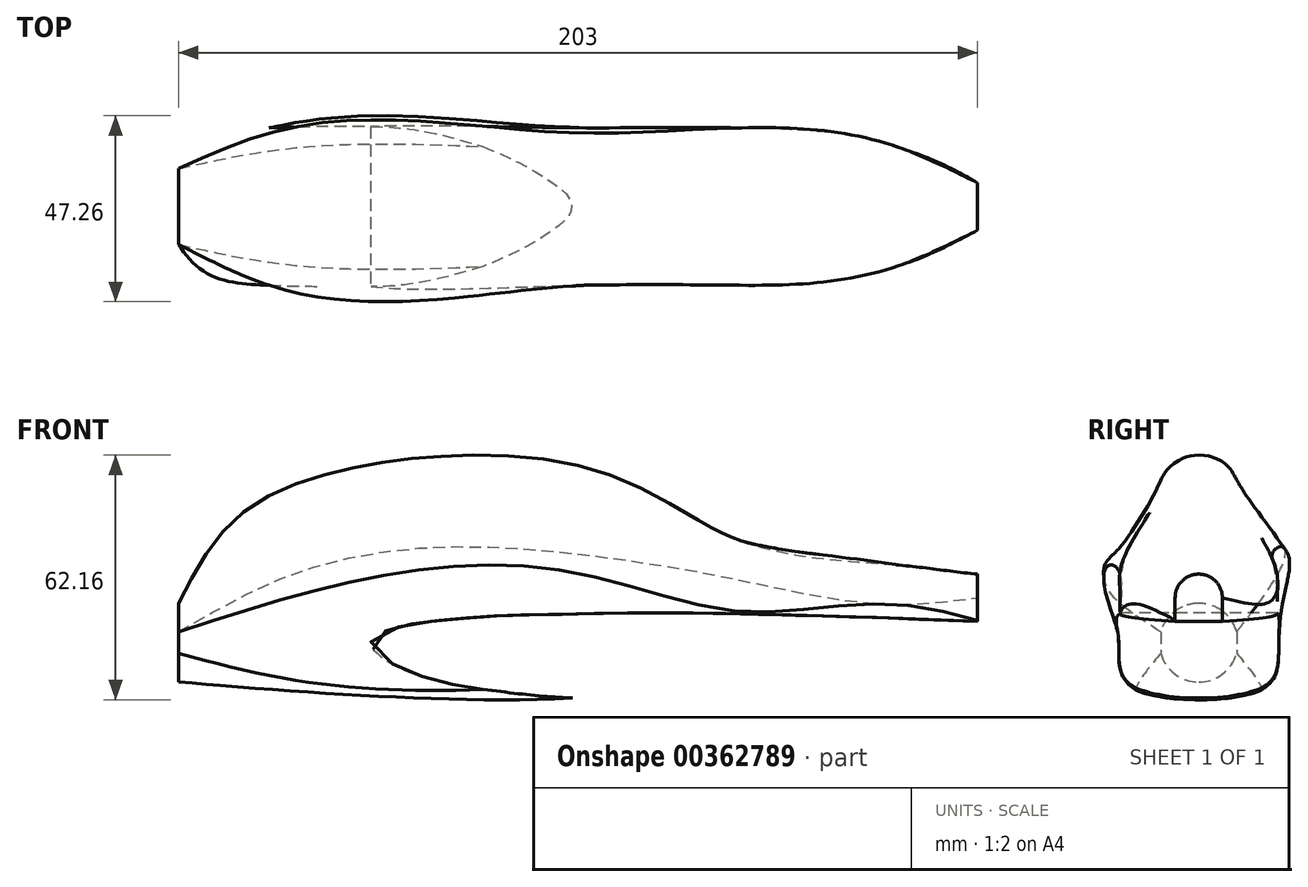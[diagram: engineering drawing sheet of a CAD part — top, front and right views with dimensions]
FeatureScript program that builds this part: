
annotation { "Feature Type Name" : "Feature", "Feature Type Description" : "" }
export const myFeature = defineFeature(function(context is Context, id is Id, definition is map)
    precondition{}
    {
        {
            var Q0;
            Q0=qCreatedBy(makeId("Front.planeOp"),FACE);
            var sketch = newSketch(context, id + "F0", { "sketchPlane" : qUnion([Q0])});
            skLineSegment(sketch, "E0", {"start": v(0, 0) * mm, "end": v(80, 0) * mm});
            skLineSegment(sketch, "E1", {"start": v(80, 0) * mm, "end": v(120, 0) * mm});
            skLineSegment(sketch, "E2", {"start": v(120, 0) * mm, "end": v(160, 0) * mm});
            skLineSegment(sketch, "E3", {"start": v(0, 0) * mm, "end": v(-23, 0) * mm});
            skFitSpline(sketch, "E4.MirrorC", {"points": [v(25.84, 0.14) * mm, v(26.2, -1.34) * mm, v(27.08, -2.35) * mm, v(28.33, -3.55) * mm, v(30.08, -4.7) * mm, v(32.8, -6.23) * mm, v(35.46, -7.4) * mm, v(38.11, -8.38) * mm, v(44.79, -10.16) * mm, v(48.42, -10.93) * mm, v(53, -11.66) * mm, v(60.13, -12.6) * mm, v(65.7, -13.23) * mm, v(74.41, -13.95) * mm, v(88.1, -14.27) * mm, v(105.53, -14.11) * mm, v(121.93, -13.31) * mm, v(140.09, -12.11) * mm, v(156.97, -10.83) * mm, v(169.9, -9.7) * mm, v(184.03, -8.35) * mm, v(203.13, -6.33) * mm, v(218.47, -4.65) * mm, v(234.68, -3.1) * mm, v(252.9, -1.42) * mm, v(264.8, -0.42) * mm, v(275.84, 0.12) * mm, v(266.91, 0.53) * mm, v(261.43, 0.73) * mm, v(246.9, 1.7) * mm, v(235.2, 2.49) * mm, v(226.11, 3) * mm, v(209.6, 3.97) * mm, v(191.03, 4.88) * mm, v(170.07, 5.75) * mm, v(159.92, 6.16) * mm, v(136, 6.9) * mm, v(118.1, 7.34) * mm, v(93.27, 7.6) * mm, v(84.17, 7.42) * mm, v(60.8, 6.9) * mm, v(51, 6.34) * mm, v(44.7, 5.78) * mm, v(38.68, 5.1) * mm, v(33.53, 4.18) * mm, v(29.5, 2.94) * mm, v(27.61, 2.16) * mm, v(26.44, 1.4) * mm, v(25.84, 0.14) * mm]});
            skLineSegment(sketch, "E5", {"start": v(160, 0) * mm, "end": v(180, 0) * mm});
            skSolve(sketch);
        }
        {
            var Q0;
            Q0=sQuery(id+"F0.wireOp",EDGE,"E0");
            var Q1;
            Q1=sQuery(id+"F0.wireOp",VERTEX,"E1.start");
            cPlane(context, id + "F1", {"entities" : qUnion([Q0, Q1]), "cplaneType" : CPlaneType.LINE_POINT, "offset" : 25 * mm, "width" : 150 * mm, "height" : 150 * mm});
        }
        {
            var Q0;
            Q0=sQuery(id+"F0.wireOp",EDGE,"E1");
            var Q1;
            Q1=sQuery(id+"F0.wireOp",VERTEX,"E2.start");
            cPlane(context, id + "F2", {"entities" : qUnion([Q0, Q1]), "cplaneType" : CPlaneType.LINE_POINT, "offset" : 25 * mm, "width" : 150 * mm, "height" : 150 * mm});
        }
        {
            var Q0;
            Q0=sQuery(id+"F0.wireOp",EDGE,"E2");
            var Q1;
            Q1=sQuery(id+"F0.wireOp",VERTEX,"E2.end");
            cPlane(context, id + "F3", {"entities" : qUnion([Q0, Q1]), "cplaneType" : CPlaneType.LINE_POINT, "offset" : 25 * mm, "width" : 150 * mm, "height" : 150 * mm});
        }
        {
            var Q0;
            Q0=sQuery(id+"F0.wireOp",EDGE,"E3");
            var Q1;
            Q1=sQuery(id+"F0.wireOp",VERTEX,"E3.end");
            cPlane(context, id + "F4", {"entities" : qUnion([Q0, Q1]), "cplaneType" : CPlaneType.LINE_POINT, "offset" : 25 * mm, "width" : 150 * mm, "height" : 150 * mm});
        }
        {
            var Q0;
            Q0=qCreatedBy(id+"F4.planeOp",FACE);
            var sketch = newSketch(context, id + "F5", { "sketchPlane" : qUnion([Q0])});
            skArc(sketch, "E6", {"start": v(0, 10) * mm, "mid": v(-6.04, 7.97) * mm, "end": v(-9.63, 2.7) * mm});
            skArc(sketch, "E7", {"start": v(0, -10) * mm, "mid": v(-6.04, -7.97) * mm, "end": v(-9.63, -2.7) * mm});
            skLineSegment(sketch, "E8", {"start": v(-9.63, 2.7) * mm, "end": v(-9.63, -2.7) * mm});
            skPoint(sketch, "E9", {"position": v(-9.63, 0) * mm});
            skPoint(sketch, "E9.positionSnap0", {"position": v(-9.63, 0) * mm});
            skArc(sketch, "E10.MirrorCS", {"start": v(0, -10) * mm, "mid": v(6.04, -7.97) * mm, "end": v(9.63, -2.7) * mm});
            skLineSegment(sketch, "E11.MirrorCS", {"start": v(9.63, 2.7) * mm, "end": v(9.63, -2.7) * mm});
            skArc(sketch, "E12.MirrorCS", {"start": v(0, 10) * mm, "mid": v(6.04, 7.97) * mm, "end": v(9.63, 2.7) * mm});
            skSolve(sketch);
        }
        {
            var Q0;
            Q0=qCreatedBy(makeId("Right.planeOp"),FACE);
            var sketch = newSketch(context, id + "F6", { "sketchPlane" : qUnion([Q0])});
            skArc(sketch, "E13", {"start": v(20, 10) * mm, "mid": v(19.66, 12.59) * mm, "end": v(18.66, 15) * mm});
            skArc(sketch, "E14", {"start": v(8.66, 32.32) * mm, "mid": v(5, 35.98) * mm, "end": v(0, 37.32) * mm});
            skLineSegment(sketch, "E15", {"start": v(18.66, 15) * mm, "end": v(8.66, 32.32) * mm});
            skLineSegment(sketch, "E16", {"start": v(20, 0) * mm, "end": v(20, 10) * mm});
            skEllipticalArc(sketch, "E17", {});
            skPoint(sketch, "E18", {"position": v(0, 37.32) * mm});
            skPoint(sketch, "E19.end.orphan", {"position": v(-20, 0) * mm});
            skPoint(sketch, "E20.center.orphan", {"position": v(-10, 10) * mm});
            skEllipticalArc(sketch, "E21.MirrorCS", {});
            skLineSegment(sketch, "E22.MirrorCS", {"start": v(-20, 0) * mm, "end": v(-20, 10) * mm});
            skArc(sketch, "E23.MirrorCS", {"start": v(-20, 10) * mm, "mid": v(-19.66, 12.59) * mm, "end": v(-18.66, 15) * mm});
            skLineSegment(sketch, "E24.MirrorCS", {"start": v(-18.66, 15) * mm, "end": v(-8.66, 32.32) * mm});
            skArc(sketch, "E25.MirrorCS", {"start": v(-8.66, 32.32) * mm, "mid": v(-5, 35.98) * mm, "end": v(0, 37.32) * mm});
            const initialGuessF6  = {"E17": [0, 0, -1, 0, 0.02, 0.011848411419733682, 1.5707963267948966, 3.141592653589793], "E21.MirrorCS": [0, 0, 1, 0, 0.02, 0.011848411419733682, 3.141592653589793, 4.71238898038469]};
            skSetInitialGuess(sketch, initialGuessF6);
            skSolve(sketch);
        }
        {
            var Q0;
            Q0=qCreatedBy(id+"F1.planeOp",FACE);
            var sketch = newSketch(context, id + "F7", { "sketchPlane" : qUnion([Q0])});
            skArc(sketch, "E26", {"start": v(20, 17.34) * mm, "mid": v(19.66, 19.93) * mm, "end": v(18.66, 22.34) * mm});
            skArc(sketch, "E27", {"start": v(8.66, 39.66) * mm, "mid": v(5, 43.32) * mm, "end": v(0, 44.66) * mm});
            skLineSegment(sketch, "E28", {"start": v(18.66, 22.34) * mm, "end": v(8.66, 39.66) * mm});
            skLineSegment(sketch, "E29", {"start": v(20, 0) * mm, "end": v(20, 17.34) * mm});
            skPoint(sketch, "E30", {"position": v(0, 0) * mm});
            skPoint(sketch, "E31", {"position": v(0, 7.34) * mm});
            skEllipticalArc(sketch, "E32", {});
            skPoint(sketch, "E33", {"position": v(0, 44.66) * mm});
            skPoint(sketch, "E34.end.orphan", {"position": v(-20, 0) * mm});
            skEllipticalArc(sketch, "E35.MirrorCS", {});
            skLineSegment(sketch, "E36.MirrorCS", {"start": v(-20, 0) * mm, "end": v(-20, 17.34) * mm});
            skArc(sketch, "E37.MirrorCS", {"start": v(-20, 17.34) * mm, "mid": v(-19.66, 19.93) * mm, "end": v(-18.66, 22.34) * mm});
            skLineSegment(sketch, "E38.MirrorCS", {"start": v(-18.66, 22.34) * mm, "end": v(-8.66, 39.66) * mm});
            skArc(sketch, "E39.MirrorCS", {"start": v(-8.66, 39.66) * mm, "mid": v(-5, 43.32) * mm, "end": v(0, 44.66) * mm});
            const initialGuessF7  = {"E32": [0, 0, 1, 0, 0.02, 0.013871131549420329, 4.71238898038469, 0], "E35.MirrorCS": [0, 0, -1, 0, 0.02, 0.013871131549420329, 0, 1.5707963267948966]};
            skSetInitialGuess(sketch, initialGuessF7);
            skSolve(sketch);
        }
        {
            var Q0;
            Q0=qCreatedBy(id+"F2.planeOp",FACE);
            var sketch = newSketch(context, id + "F8", { "sketchPlane" : qUnion([Q0])});
            skLineSegment(sketch, "E40", {"start": v(0, 25.82) * mm, "end": v(10, 25.82) * mm});
            skLineSegment(sketch, "E41", {"start": v(20, 15.82) * mm, "end": v(20, 0) * mm});
            skPoint(sketch, "E42", {"position": v(0, 0) * mm});
            skArc(sketch, "E43", {"start": v(20, 15.82) * mm, "mid": v(17.07, 22.89) * mm, "end": v(10, 25.82) * mm});
            skPoint(sketch, "E44.orphan", {"position": v(20, 25.82) * mm});
            skPoint(sketch, "E45.orphan", {"position": v(-20, 25.82) * mm});
            skPoint(sketch, "E46.start.orphan", {"position": v(-20, 0) * mm});
            skPoint(sketch, "E47.orphan", {"position": v(-10, 25.82) * mm});
            skEllipticalArc(sketch, "E48", {});
            skEllipticalArc(sketch, "E49.MirrorCS", {});
            skLineSegment(sketch, "E50.MirrorCS", {"start": v(-20, 15.82) * mm, "end": v(-20, 0) * mm});
            skArc(sketch, "E51.MirrorCS", {"start": v(-20, 15.82) * mm, "mid": v(-17.07, 22.89) * mm, "end": v(-10, 25.82) * mm});
            skLineSegment(sketch, "E52.MirrorCS", {"start": v(0, 25.82) * mm, "end": v(-10, 25.82) * mm});
            const initialGuessF8  = {"E48": [0, 0, 1, 0, 0.02, 0.007889031401392533, 4.71238898038469, 0], "E49.MirrorCS": [0, 0, -1, 0, 0.02, 0.007889031401392533, 0, 1.5707963267948966]};
            skSetInitialGuess(sketch, initialGuessF8);
            skSolve(sketch);
        }
        {
            var Q0;
            Q0=qCreatedBy(id+"F3.planeOp",FACE);
            var sketch = newSketch(context, id + "F9", { "sketchPlane" : qUnion([Q0])});
            skLineSegment(sketch, "E53", {"start": v(0, 19.7) * mm, "end": v(5, 19.7) * mm});
            skLineSegment(sketch, "E54", {"start": v(15, 9.7) * mm, "end": v(15, 0) * mm});
            skPoint(sketch, "E55", {"position": v(0, 0) * mm});
            skArc(sketch, "E56", {"start": v(15, 9.7) * mm, "mid": v(12.07, 16.76) * mm, "end": v(5, 19.7) * mm});
            skPoint(sketch, "E57.start.orphan", {"position": v(-15, 0) * mm});
            skPoint(sketch, "E58.orphan", {"position": v(-5, 19.7) * mm});
            skEllipticalArc(sketch, "E59", {});
            skEllipticalArc(sketch, "E60.MirrorCS", {});
            skLineSegment(sketch, "E61.MirrorCS", {"start": v(-15, 9.7) * mm, "end": v(-15, 0) * mm});
            skArc(sketch, "E62.MirrorCS", {"start": v(-15, 9.7) * mm, "mid": v(-12.07, 16.76) * mm, "end": v(-5, 19.7) * mm});
            skLineSegment(sketch, "E63.MirrorCS", {"start": v(0, 19.7) * mm, "end": v(-5, 19.7) * mm});
            const initialGuessF9  = {"E59": [0, 0, 1, 0, 0.015, 0.0073381839387434, 4.71238898038469, 0], "E60.MirrorCS": [0, 0, -1, 0, 0.015, 0.0073381839387434, 0, 1.5707963267948966]};
            skSetInitialGuess(sketch, initialGuessF9);
            skSolve(sketch);
        }
        {
            var Q0;
            Q0=sQuery(id+"F0.wireOp",EDGE,"E5");
            var Q1;
            Q1=sQuery(id+"F0.wireOp",VERTEX,"E5.end");
            cPlane(context, id + "F10", {"entities" : qUnion([Q0, Q1]), "cplaneType" : CPlaneType.LINE_POINT, "offset" : 25 * mm, "width" : 150 * mm, "height" : 150 * mm});
        }
        {
            var Q0;
            Q0=qCreatedBy(id+"F10.planeOp",FACE);
            var sketch = newSketch(context, id + "F11", { "sketchPlane" : qUnion([Q0])});
            skArc(sketch, "E64", {"start": v(6, 11.41) * mm, "mid": v(4.24, 15.65) * mm, "end": v(0, 17.41) * mm});
            skLineSegment(sketch, "E65", {"start": v(6, 0) * mm, "end": v(6, 11.41) * mm});
            skArc(sketch, "E66", {"start": v(0, -6) * mm, "mid": v(4.24, -4.24) * mm, "end": v(6, 0) * mm});
            skArc(sketch, "E67.MirrorCS", {"start": v(0, -6) * mm, "mid": v(-4.24, -4.24) * mm, "end": v(-6, 0) * mm});
            skLineSegment(sketch, "E68.MirrorCS", {"start": v(-6, 0) * mm, "end": v(-6, 11.41) * mm});
            skArc(sketch, "E69.MirrorCS", {"start": v(-6, 11.41) * mm, "mid": v(-4.24, 15.65) * mm, "end": v(0, 17.41) * mm});
            skSolve(sketch);
        }
        {
            var Q0;
            Q0=qCreatedBy(makeId("Top.planeOp"),FACE);
            var sketch = newSketch(context, id + "F12", { "sketchPlane" : qUnion([Q0])});
            skFitSpline(sketch, "E70", {"points": [v(-23, 9.63) * mm, v(0, 20) * mm, v(80, 20) * mm, v(120, 20) * mm, v(160, 15) * mm, v(180, 6) * mm], "startDerivative": vector(109.79, 168.65) * mm, "endDerivative": vector(136.65, -101.2) * mm});
            skFitSpline(sketch, "E71.MirrorCS", {"points": [v(-23, -9.63) * mm, v(0, -20) * mm, v(80, -20) * mm, v(120, -20) * mm, v(160, -15) * mm, v(180, -6) * mm], "startDerivative": vector(109.79, -168.65) * mm, "endDerivative": vector(136.65, 101.2) * mm});
            skSolve(sketch);
        }
        {
            var Q0;
            Q0=qCreatedBy(makeId("Front.planeOp"),FACE);
            var sketch = newSketch(context, id + "F13", { "sketchPlane" : qUnion([Q0])});
            skFitSpline(sketch, "E72", {"points": [v(-23, -10) * mm, v(0, -11.85) * mm, v(80, -13.87) * mm, v(120, -7.89) * mm, v(160, -7.34) * mm, v(180, -6) * mm], "startDerivative": vector(131.62, -10.02) * mm, "endDerivative": vector(123.76, 18.36) * mm});
            skFitSpline(sketch, "E73", {"points": [v(-23, 10) * mm, v(0, 37.32) * mm, v(80, 44.66) * mm, v(120, 25.82) * mm, v(160, 19.7) * mm, v(180, 17.41) * mm], "startDerivative": vector(93.32, 179.4) * mm, "endDerivative": vector(141.15, -12.46) * mm});
            skSolve(sketch);
        }
        {
            var Q0;
            Q0=makeQuery(id+"F5.imprint","IMPRINT",FACE,{"disambiguationData":[TD([[makeQuery(id+"F5.imprint","IMPRINT",EDGE,{"derivedFrom":sQuery(id+"F5.wireOp",EDGE,"E6")}),1.0]])]});
            var Q1;
            Q1=makeQuery(id+"F6.imprint","IMPRINT",FACE,{"disambiguationData":[TD([[makeQuery(id+"F6.imprint","IMPRINT",EDGE,{"derivedFrom":sQuery(id+"F6.wireOp",EDGE,"E13")}),1.0]])]});
            var Q2;
            Q2=makeQuery(id+"F7.imprint","IMPRINT",FACE,{"disambiguationData":[TD([[makeQuery(id+"F7.imprint","IMPRINT",EDGE,{"derivedFrom":sQuery(id+"F7.wireOp",EDGE,"E26")}),1.0]])]});
            var Q3;
            Q3=makeQuery(id+"F8.imprint","IMPRINT",FACE,{"disambiguationData":[TD([[makeQuery(id+"F8.imprint","IMPRINT",EDGE,{"derivedFrom":sQuery(id+"F8.wireOp",EDGE,"E40")}),-1.0]])]});
            var Q4;
            Q4=makeQuery(id+"F9.imprint","IMPRINT",FACE,{"disambiguationData":[TD([[makeQuery(id+"F9.imprint","IMPRINT",EDGE,{"derivedFrom":sQuery(id+"F9.wireOp",EDGE,"E53")}),-1.0]])]});
            var Q5;
            Q5=makeQuery(id+"F11.imprint","IMPRINT",FACE,{"disambiguationData":[TD([[makeQuery(id+"F11.imprint","IMPRINT",EDGE,{"derivedFrom":sQuery(id+"F11.wireOp",EDGE,"E64")}),1.0]])]});
            var Q6;
            Q6=sQuery(id+"F12.wireOp",EDGE,"E71.MirrorCS");
            var Q7;
            Q7=sQuery(id+"F12.wireOp",EDGE,"E70");
            var Q8;
            Q8=sQuery(id+"F13.wireOp",EDGE,"E72");
            var Q9;
            Q9=sQuery(id+"F13.wireOp",EDGE,"E73");
            loft(context, id + "F14", {"addGuides" : true, "sheetProfilesArray" : [{ "sheetProfileEntities" : qUnion([Q0]) }, { "sheetProfileEntities" : qUnion([Q1]) }, { "sheetProfileEntities" : qUnion([Q2]) }, { "sheetProfileEntities" : qUnion([Q3]) }, { "sheetProfileEntities" : qUnion([Q4]) }, { "sheetProfileEntities" : qUnion([Q5]) }], "guidesArray" : [{ "guideEntities" : qUnion([Q6]), "guideDerivativeType" : LoftGuideDerivativeType.DEFAULT, "guideDerivativeMagnitude" : 1 }, { "guideEntities" : qUnion([Q7]), "guideDerivativeType" : LoftGuideDerivativeType.DEFAULT, "guideDerivativeMagnitude" : 1 }, { "guideEntities" : qUnion([Q8]), "guideDerivativeType" : LoftGuideDerivativeType.DEFAULT, "guideDerivativeMagnitude" : 1 }, { "guideEntities" : qUnion([Q9]), "guideDerivativeType" : LoftGuideDerivativeType.DEFAULT, "guideDerivativeMagnitude" : 1 }]});
        }
        {
            var Q0;
            Q0=makeQuery(id+"F0.imprint","IMPRINT",FACE,{"disambiguationData":[TD([[makeQuery(id+"F0.imprint","IMPRINT",EDGE,{"derivedFrom":sQuery(id+"F0.wireOp",EDGE,"E4.MirrorC")}),1.0]])]});
            extrude(context, id + "F15", {"entities" : qUnion([Q0]), "operationType" : NewBodyOperationType.REMOVE, "oppositeDirection" : true, "depth" : 50 * mm, "hasSecondDirection" : true, "secondDirectionOppositeDirection" : false, "secondDirectionDepth" : 50 * mm});
        }
    });
